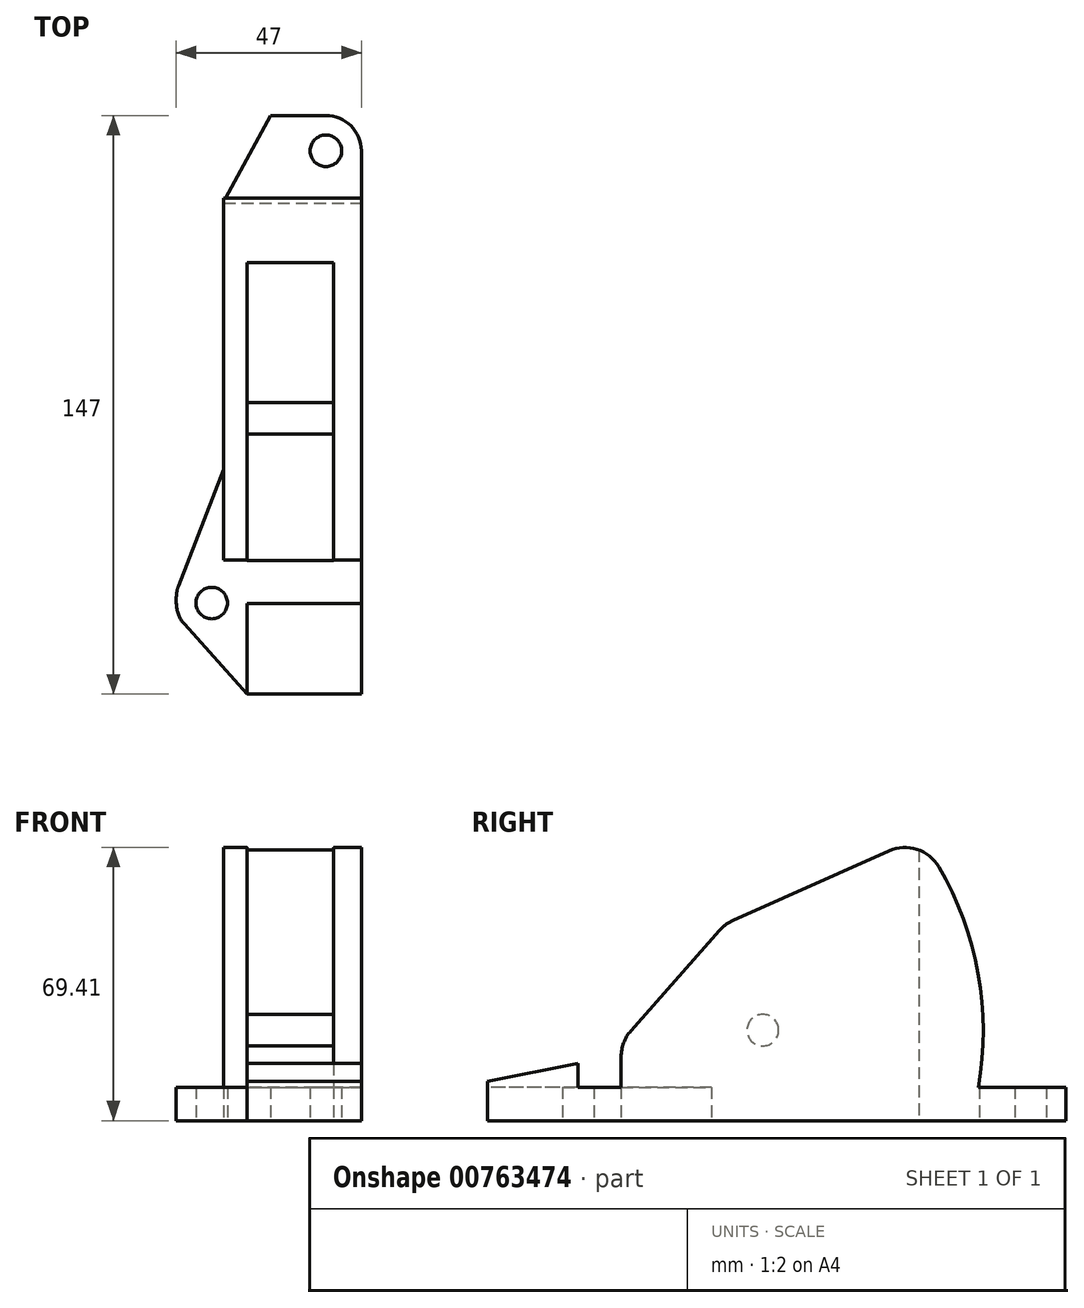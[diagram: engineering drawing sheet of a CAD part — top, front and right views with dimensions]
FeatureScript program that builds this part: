
annotation { "Feature Type Name" : "Feature", "Feature Type Description" : "" }
export const myFeature = defineFeature(function(context is Context, id is Id, definition is map)
    precondition{}
    {
        {
            var Q0;
            Q0=qCreatedBy(makeId("Top.planeOp"),FACE);
            var sketch = newSketch(context, id + "F0", { "sketchPlane" : qUnion([Q0])});
            skLineSegment(sketch, "E0.bottom", {"start": v(0, 0) * mm, "end": v(35, 0) * mm});
            skLineSegment(sketch, "E0.left", {"start": v(0, 0) * mm, "end": v(0, 68) * mm});
            skLineSegment(sketch, "E0.right", {"start": v(35, 0) * mm, "end": v(35, 68) * mm});
            skCircle(sketch, "E1", {"center": v(26, 81) * mm, "radius": 4 * mm});
            skLineSegment(sketch, "E2", {"start": v(0, 68) * mm, "end": v(12, 90) * mm});
            skLineSegment(sketch, "E3", {"start": v(12, 90) * mm, "end": v(26, 90) * mm});
            skArc(sketch, "E4", {"start": v(35, 81) * mm, "mid": v(32.36, 87.36) * mm, "end": v(26, 90) * mm});
            skLineSegment(sketch, "E5", {"start": v(35, 81) * mm, "end": v(35, 68) * mm});
            skLineSegment(sketch, "E6", {"start": v(0, 0) * mm, "end": v(-12, -31) * mm});
            skLineSegment(sketch, "E7", {"start": v(-12, -31) * mm, "end": v(-12, -37) * mm});
            skLineSegment(sketch, "E8", {"start": v(-12, -37) * mm, "end": v(6, -57) * mm});
            skLineSegment(sketch, "E9", {"start": v(6, -57) * mm, "end": v(35, -57) * mm});
            skLineSegment(sketch, "E10", {"start": v(35, -57) * mm, "end": v(35, 0) * mm});
            skCircle(sketch, "E11", {"center": v(-3, -33.9) * mm, "radius": 4 * mm});
            skSolve(sketch);
        }
        {
            var Q0;
            Q0=makeQuery(id+"F0.imprint","IMPRINT",FACE,{"disambiguationData":[TD([[makeQuery(id+"F0.imprint","IMPRINT",EDGE,{"derivedFrom":sQuery(id+"F0.wireOp",EDGE,"E0.bottom")}),1.0]])]});
            var Q1;
            Q1=makeQuery(id+"F0.imprint","IMPRINT",FACE,{"disambiguationData":[TD([[makeQuery(id+"F0.imprint","IMPRINT",EDGE,{"derivedFrom":sQuery(id+"F0.wireOp",EDGE,"E0.bottom")}),-1.0]])]});
            extrude(context, id + "F1", {"entities" : qUnion([Q0, Q1]), "depth" : 8.5 * mm, "offsetDistance" : 25 * mm});
        }
        {
            var Q0;
            Q0=makeQuery(id+"F1.opExtrude","SWEPT_EDGE",EDGE,{"disambiguationData":[OSD([sQuery(id+"F0.wireOp",EDGE,"E7"),sQuery(id+"F0.wireOp",EDGE,"E8")])]});
            var Q1;
            Q1=makeQuery(id+"F1.opExtrude","SWEPT_EDGE",EDGE,{"disambiguationData":[OSD([sQuery(id+"F0.wireOp",EDGE,"E6"),sQuery(id+"F0.wireOp",EDGE,"E7")])]});
            fillet(context, id + "F2", {"entities" : qUnion([Q0, Q1]), "radius" : 8 * mm, "tangentPropagation" : true, "allowEdgeOverflow" : false});
        }
        {
            var Q0;
            Q0=makeQuery(id+"F1.opExtrude","SWEPT_FACE",FACE,{"disambiguationData":[OSD([sQuery(id+"F0.wireOp",EDGE,"E0.right"),sQuery(id+"F0.wireOp",EDGE,"E5"),sQuery(id+"F0.wireOp",EDGE,"E10")])]});
            var sketch = newSketch(context, id + "F3", { "sketchPlane" : qUnion([Q0])});
            skPoint(sketch, "E12", {"position": v(-57, 0) * mm});
            skLineSegment(sketch, "E13", {"start": v(-57, 0) * mm, "end": v(-57, 10) * mm});
            skLineSegment(sketch, "E14", {"start": v(-57, 10) * mm, "end": v(-34, 14.5) * mm});
            skLineSegment(sketch, "E15", {"start": v(-34, 14.5) * mm, "end": v(-34, 0) * mm});
            skLineSegment(sketch, "E16", {"start": v(-34, 0) * mm, "end": v(-57, 0) * mm});
            skSolve(sketch);
        }
        {
            var Q0;
            Q0 = qSketchRegion(id + "F3", true);
            var Q1;
            Q1=makeQuery(id+"F1.opExtrude","CAP_VERTEX",VERTEX,{"disambiguationData":[OSD([sQuery(id+"F0.wireOp",EDGE,"E8"),sQuery(id+"F0.wireOp",EDGE,"E9")])],"isStart":false});
            extrude(context, id + "F4", {"entities" : qUnion([Q0]), "operationType" : NewBodyOperationType.ADD, "endBound" : BoundingType.UP_TO_VERTEX, "oppositeDirection" : true, "depth" : 25 * mm, "endBoundEntityVertex" : qUnion([Q1]), "offsetDistance" : 25 * mm});
        }
        {
            var Q0;
            Q0=makeQuery(id+"F4.boolean.opBoolean","MERGE",FACE,{"derivedFrom":[makeQuery(id+"F1.opExtrude","SWEPT_FACE",FACE,{"disambiguationData":[OSD([sQuery(id+"F0.wireOp",EDGE,"E0.right"),sQuery(id+"F0.wireOp",EDGE,"E5"),sQuery(id+"F0.wireOp",EDGE,"E10")])]}),makeQuery(id+"F4.opExtrude","CAP_FACE",FACE,{"disambiguationData":[OSD([sQuery(id+"F3.wireOp",EDGE,"E13"),sQuery(id+"F3.wireOp",EDGE,"E14"),sQuery(id+"F3.wireOp",EDGE,"E15"),sQuery(id+"F3.wireOp",EDGE,"E16")])],"isStart":true})]});
            var sketch = newSketch(context, id + "F5", { "sketchPlane" : qUnion([Q0])});
            skPoint(sketch, "E17", {"position": v(13, 0) * mm});
            skLineSegment(sketch, "E18", {"start": v(13, 0) * mm, "end": v(13, 23) * mm, "construction": true});
            skCircle(sketch, "E19", {"center": v(13, 23) * mm, "radius": 13.54 * mm, "construction": true});
            skPoint(sketch, "E20", {"position": v(-23, 0) * mm});
            skLineSegment(sketch, "E21", {"start": v(-23, 0) * mm, "end": v(-23, 20) * mm});
            skLineSegment(sketch, "E22", {"start": v(-23, 20) * mm, "end": v(3.46, 50) * mm});
            skLineSegment(sketch, "E23", {"start": v(3.46, 50) * mm, "end": v(52.77, 72) * mm});
            skArc(sketch, "E24", {"start": v(67.77, 8.5) * mm, "mid": v(66.78, 41.79) * mm, "end": v(52.77, 72) * mm});
            skPoint(sketch, "E24.second.point", {"position": v(67.77, 8.5) * mm});
            skPoint(sketch, "E24.third.point", {"position": v(63.45, 52.56) * mm});
            skLineSegment(sketch, "E25", {"start": v(-23, 0) * mm, "end": v(67.77, 8.5) * mm});
            skCircle(sketch, "E26", {"center": v(13, 23) * mm, "radius": 4 * mm});
            skSolve(sketch);
        }
        {
            var Q0;
            {var subQ4=sQuery(id+"F5.wireOp",EDGE,"E22");Q0=makeQuery(id+"F5.imprint","IMPRINT",FACE,{"disambiguationData":[TD([[makeQuery(id+"F5.imprint","IMPRINT",EDGE,{"derivedFrom":subQ4}),-1.0]])]});}
            var Q1;
            Q1=makeQuery(id+"F1.opExtrude","SWEPT_FACE",FACE,{"disambiguationData":[OSD([sQuery(id+"F0.wireOp",EDGE,"E0.left")])]});
            extrude(context, id + "F6", {"entities" : qUnion([Q0]), "operationType" : NewBodyOperationType.ADD, "endBound" : BoundingType.UP_TO_SURFACE, "oppositeDirection" : true, "depth" : 25 * mm, "endBoundEntityFace" : qUnion([Q1]), "offsetDistance" : 25 * mm});
        }
        {
            var Q0;
            Q0=qCreatedBy(makeId("Top.planeOp"),FACE);
            var sketch = newSketch(context, id + "F7", { "sketchPlane" : qUnion([Q0])});
            skLineSegment(sketch, "E27.bottom", {"start": v(6, 52.6) * mm, "end": v(28, 52.6) * mm});
            skLineSegment(sketch, "E27.top", {"start": v(6, -23.06) * mm, "end": v(28, -23.06) * mm});
            skLineSegment(sketch, "E27.left", {"start": v(6, 52.6) * mm, "end": v(6, -23.06) * mm});
            skLineSegment(sketch, "E27.right", {"start": v(28, 52.6) * mm, "end": v(28, -23.06) * mm});
            skSolve(sketch);
        }
        {
            var Q0;
            Q0=makeQuery(id+"F7.imprint","IMPRINT",FACE,{"disambiguationData":[TD([[makeQuery(id+"F7.imprint","IMPRINT",EDGE,{"derivedFrom":sQuery(id+"F7.wireOp",EDGE,"E27.bottom")}),-1.0]])]});
            extrude(context, id + "F8", {"entities" : qUnion([Q0]), "operationType" : NewBodyOperationType.REMOVE, "endBound" : BoundingType.THROUGH_ALL, "depth" : 25 * mm, "offsetDistance" : 25 * mm});
        }
        {
            var Q0;
            Q0=makeQuery(id+"F5.imprint","IMPRINT",FACE,{"disambiguationData":[TD([[makeQuery(id+"F5.imprint","IMPRINT",EDGE,{"derivedFrom":sQuery(id+"F5.wireOp",EDGE,"E26")}),1.0]])]});
            var Q1;
            {var subQ0=sQuery(id+"F0.wireOp",EDGE,"E0.left");Q1=makeQuery(id+"F6.boolean.opBoolean","MERGE",FACE,{"derivedFrom":[makeQuery(id+"F1.opExtrude","SWEPT_FACE",FACE,{"disambiguationData":[OSD([subQ0])]}),makeQuery(id+"F6.opExtrude","CAP_FACE",FACE,{"disambiguationData":[OSD([subQ0])],"isStart":false})]});}
            extrude(context, id + "F9", {"entities" : qUnion([Q0]), "operationType" : NewBodyOperationType.ADD, "endBound" : BoundingType.UP_TO_SURFACE, "oppositeDirection" : true, "depth" : 25 * mm, "endBoundEntityFace" : qUnion([Q1]), "offsetDistance" : 25 * mm});
        }
        {
            var Q0;
            Q0=makeQuery(id+"F6.opExtrude","SWEPT_EDGE",EDGE,{"disambiguationData":[OSD([sQuery(id+"F5.wireOp",EDGE,"E23"),sQuery(id+"F5.wireOp",EDGE,"E24")])]});
            var Q1;
            {var subQ0=sQuery(id+"F5.wireOp",EDGE,"E23");var subQ1=sQuery(id+"F5.wireOp",EDGE,"E22");Q1=makeQuery(id+"F8.boolean.opBoolean","SPLIT",EDGE,{"disambiguationData":[TD([makeQuery(id+"F8.opExtrude","SWEPT_FACE",FACE,{"disambiguationData":[OSD([sQuery(id+"F7.wireOp",EDGE,"E27.right")])]})])],"derivedFrom":makeQuery(id+"F6.opExtrude","SWEPT_EDGE",EDGE,{"disambiguationData":[OSD([subQ1,subQ0])]})});}
            var Q2;
            {var subQ0=sQuery(id+"F5.wireOp",EDGE,"E23");var subQ1=sQuery(id+"F0.wireOp",EDGE,"E0.left");var subQ2=sQuery(id+"F5.wireOp",EDGE,"E22");Q2=makeQuery(id+"F8.boolean.opBoolean","SPLIT",EDGE,{"disambiguationData":[TD([makeQuery(id+"F1.opExtrude","SWEPT_FACE",FACE,{"disambiguationData":[OSD([subQ1])]})])],"derivedFrom":makeQuery(id+"F6.opExtrude","SWEPT_EDGE",EDGE,{"disambiguationData":[OSD([subQ2,subQ0])]})});}
            var Q3;
            {var subQ0=sQuery(id+"F5.wireOp",EDGE,"E22");var subQ1=sQuery(id+"F5.wireOp",EDGE,"E21");Q3=makeQuery(id+"F8.boolean.opBoolean","SPLIT",EDGE,{"disambiguationData":[TD([makeQuery(id+"F8.opExtrude","SWEPT_FACE",FACE,{"disambiguationData":[OSD([sQuery(id+"F7.wireOp",EDGE,"E27.right")])]})])],"derivedFrom":makeQuery(id+"F6.opExtrude","SWEPT_EDGE",EDGE,{"disambiguationData":[OSD([subQ1,subQ0])]})});}
            var Q4;
            {var subQ0=sQuery(id+"F5.wireOp",EDGE,"E22");var subQ1=sQuery(id+"F5.wireOp",EDGE,"E21");var subQ2=sQuery(id+"F0.wireOp",EDGE,"E0.left");Q4=makeQuery(id+"F8.boolean.opBoolean","SPLIT",EDGE,{"disambiguationData":[TD([makeQuery(id+"F1.opExtrude","SWEPT_FACE",FACE,{"disambiguationData":[OSD([subQ2])]})])],"derivedFrom":makeQuery(id+"F6.opExtrude","SWEPT_EDGE",EDGE,{"disambiguationData":[OSD([subQ1,subQ0])]})});}
            fillet(context, id + "F10", {"entities" : qUnion([Q0, Q1, Q2, Q3, Q4]), "radius" : 10 * mm, "tangentPropagation" : true, "allowEdgeOverflow" : false});
        }
    });
